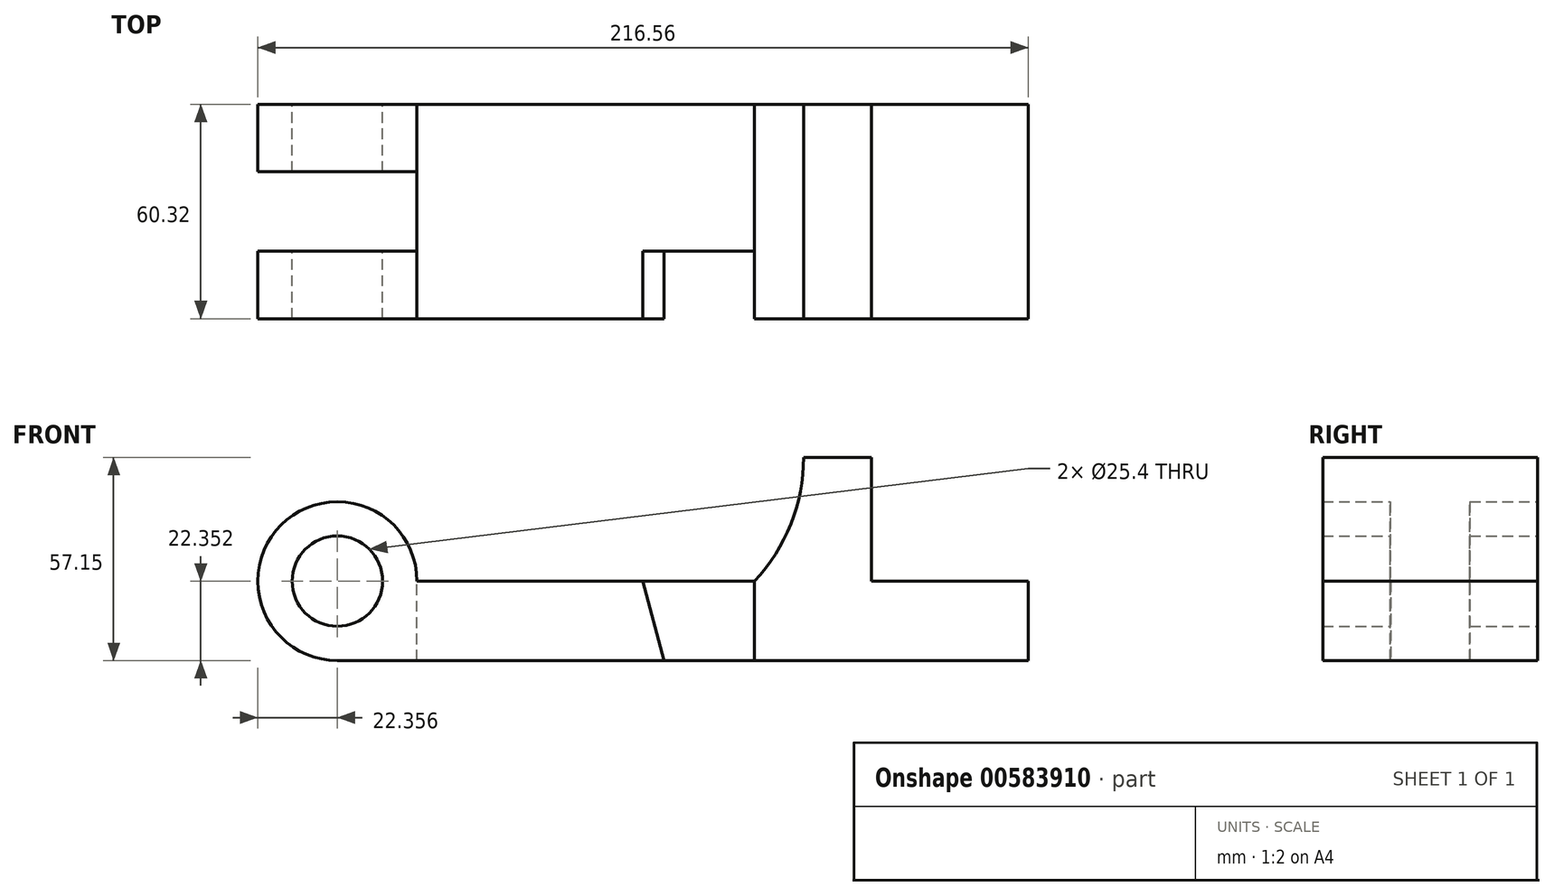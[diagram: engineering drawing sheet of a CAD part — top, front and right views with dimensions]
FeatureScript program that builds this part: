
annotation { "Feature Type Name" : "Feature", "Feature Type Description" : "" }
export const myFeature = defineFeature(function(context is Context, id is Id, definition is map)
    precondition{}
    {
        {
            var Q0;
            Q0=qCreatedBy(makeId("Front.planeOp"),FACE);
            var sketch = newSketch(context, id + "F0", { "sketchPlane" : qUnion([Q0])});
            skLineSegment(sketch, "E0.bottom", {"start": v(97.1, 22.35) * mm, "end": v(-97.1, 22.35) * mm});
            skLineSegment(sketch, "E0.top", {"start": v(97.1, 0) * mm, "end": v(-97.1, 0) * mm});
            skLineSegment(sketch, "E0.left", {"start": v(97.1, 22.35) * mm, "end": v(97.1, 0) * mm});
            skLineSegment(sketch, "E0.right", {"start": v(-97.1, 22.35) * mm, "end": v(-97.1, 0) * mm});
            skLineSegment(sketch, "E1.bottom", {"start": v(52.98, 22.35) * mm, "end": v(33.93, 22.35) * mm});
            skLineSegment(sketch, "E1.top", {"start": v(52.98, 57.15) * mm, "end": v(33.93, 57.15) * mm});
            skLineSegment(sketch, "E1.left", {"start": v(52.98, 22.35) * mm, "end": v(52.98, 57.15) * mm});
            skLineSegment(sketch, "E1.right", {"start": v(33.93, 22.35) * mm, "end": v(33.93, 57.15) * mm});
            skArc(sketch, "E2", {"start": v(20.14, 22.35) * mm, "mid": v(30.36, 38.43) * mm, "end": v(33.93, 57.15) * mm});
            skLineSegment(sketch, "E3", {"start": v(20.14, 22.35) * mm, "end": v(20.14, 0) * mm});
            skCircle(sketch, "E4", {"center": v(-97.1, 22.35) * mm, "radius": 22.35 * mm});
            skCircle(sketch, "E5", {"center": v(-97.1, 22.35) * mm, "radius": 12.7 * mm});
            skSolve(sketch);
        }
        {
            var Q0;
            Q0 = qSketchRegion(id + "F0", true);
            extrude(context, id + "F1", {"entities" : qUnion([Q0]), "endBound" : BoundingType.SYMMETRIC, "depth" : 60.32 * mm, "offsetDistance" : 25.4 * mm});
        }
        {
            var Q0;
            Q0=makeQuery(id+"F1.opExtrude","CAP_FACE",FACE,{"disambiguationData":[OSD([sQuery(id+"F0.wireOp",EDGE,"E0.bottom"),sQuery(id+"F0.wireOp",EDGE,"E0.top"),sQuery(id+"F0.wireOp",EDGE,"E0.left"),sQuery(id+"F0.wireOp",EDGE,"E1.top"),sQuery(id+"F0.wireOp",EDGE,"E1.left"),sQuery(id+"F0.wireOp",EDGE,"E2"),sQuery(id+"F0.wireOp",EDGE,"E4"),sQuery(id+"F0.wireOp",EDGE,"E5")])],"isStart":false});
            var sketch = newSketch(context, id + "F2", { "sketchPlane" : qUnion([Q0])});
            skLineSegment(sketch, "E6.0", {"start": v(97.1, 0) * mm, "end": v(-97.1, 0) * mm});
            skLineSegment(sketch, "E7.0", {"start": v(20.14, 22.35) * mm, "end": v(-74.75, 22.35) * mm});
            skLineSegment(sketch, "E8", {"start": v(20.14, 22.35) * mm, "end": v(20.14, 0) * mm});
            skLineSegment(sketch, "E9", {"start": v(-11.25, 22.35) * mm, "end": v(-5.26, 0) * mm});
            skLineSegment(sketch, "E10", {"start": v(-17.25, 22.35) * mm, "end": v(-11.25, 0) * mm});
            skLineSegment(sketch, "E11", {"start": v(-11.25, 22.35) * mm, "end": v(-11.25, 0) * mm});
            skCircle(sketch, "E12.0", {"center": v(-97.1, 22.35) * mm, "radius": 12.7 * mm});
            skLineSegment(sketch, "E13", {"start": v(-11.25, 22.35) * mm, "end": v(20.14, 22.35) * mm});
            skLineSegment(sketch, "E14", {"start": v(20.14, 0) * mm, "end": v(-5.26, 0) * mm});
            skSolve(sketch);
        }
        {
            var Q0;
            Q0=makeQuery(id+"F2.imprint","IMPRINT",FACE,{"disambiguationData":[TD([[makeQuery(id+"F2.imprint","IMPRINT",EDGE,{"derivedFrom":sQuery(id+"F2.wireOp",EDGE,"E8")}),-1.0]])]});
            extrude(context, id + "F3", {"entities" : qUnion([Q0]), "operationType" : NewBodyOperationType.REMOVE, "oppositeDirection" : true, "depth" : 19.05 * mm, "offsetDistance" : 25.4 * mm});
        }
        {
            var Q0;
            Q0=qCreatedBy(makeId("Top.planeOp"),FACE);
            cPlane(context, id + "F4", {"entities" : qUnion([Q0]), "cplaneType" : CPlaneType.OFFSET, "offset" : 49.53 * mm, "width" : 152.4 * mm, "height" : 152.4 * mm});
        }
        {
            var Q0;
            Q0=qCreatedBy(id+"F4.planeOp",FACE);
            var sketch = newSketch(context, id + "F5", { "sketchPlane" : qUnion([Q0])});
            skLineSegment(sketch, "E15", {"start": v(-119.46, -30.16) * mm, "end": v(-119.46, 30.16) * mm});
            skLineSegment(sketch, "E16.bottom", {"start": v(-119.46, 11.16) * mm, "end": v(-74.75, 11.16) * mm});
            skLineSegment(sketch, "E16.top", {"start": v(-119.46, -11.16) * mm, "end": v(-74.75, -11.16) * mm});
            skLineSegment(sketch, "E16.left", {"start": v(-119.46, 11.16) * mm, "end": v(-119.46, -11.16) * mm});
            skLineSegment(sketch, "E16.right", {"start": v(-74.75, 11.16) * mm, "end": v(-74.75, -11.16) * mm});
            skLineSegment(sketch, "E17", {"start": v(0, -65.48) * mm, "end": v(0, 56.55) * mm, "construction": true});
            skSolve(sketch);
        }
        {
            var Q0;
            Q0=makeQuery(id+"F5.imprint","IMPRINT",FACE,{"disambiguationData":[TD([[makeQuery(id+"F5.imprint","IMPRINT",EDGE,{"derivedFrom":sQuery(id+"F5.wireOp",EDGE,"E16.bottom")}),-1.0]])]});
            extrude(context, id + "F6", {"entities" : qUnion([Q0]), "operationType" : NewBodyOperationType.REMOVE, "endBound" : BoundingType.THROUGH_ALL, "oppositeDirection" : true, "depth" : 25.4 * mm, "offsetDistance" : 25.4 * mm});
        }
    });
